# Revit family: TP Lite Door full height
name_source: partatom
category: Doors
revit_build: Autodesk Revit Architecture 2012 (Build: 20110916_2132)
units: mm (PartAtom-declared; Revit-internal decimal feet)

## types (2) — shared parameters
Bottom Profile = Yes
Door offset = 35 mm  [stored 0.114829 ft]
Function = Interior
Glass panel material = Triplan Glass
Handle Height = 1000 mm  [stored 3.28084 ft]
Handle Horizontal Offest = 60 mm  [stored 0.19685 ft]
Profile material = Triplan Metal - Eloxeret Aluminium
Thickness = 25 mm  [stored 0.082021 ft]
URL = http://www.triplan.net
zero-valued in all types: Door leaf Width, Explode object

## per-type parameters (varying)
| type | Assembly Code | Door Handle Type | Door leaf material | Door leaf offset | Door leaf thickness | Manufacturer |
| Glass door |  | 2 | Triplan Glass | 2 mm  [stored 0.00656168 ft] | 20 mm  [stored 0.0656168 ft] | Triplan International A/S |
| Massive door | C1020300 | 1 | Triplan Door - NCS 0502Y | 12 mm  [stored 0.0393701 ft] | 40 mm  [stored 0.131234 ft] | Triplan International |

note: [stored X ft] marks values corroborated as IEEE doubles in the binary element streams (Revit-internal decimal feet)

## geometry (parser evidence)
native form markers: Sweep x6
no freeform markers — native parametric forms only
